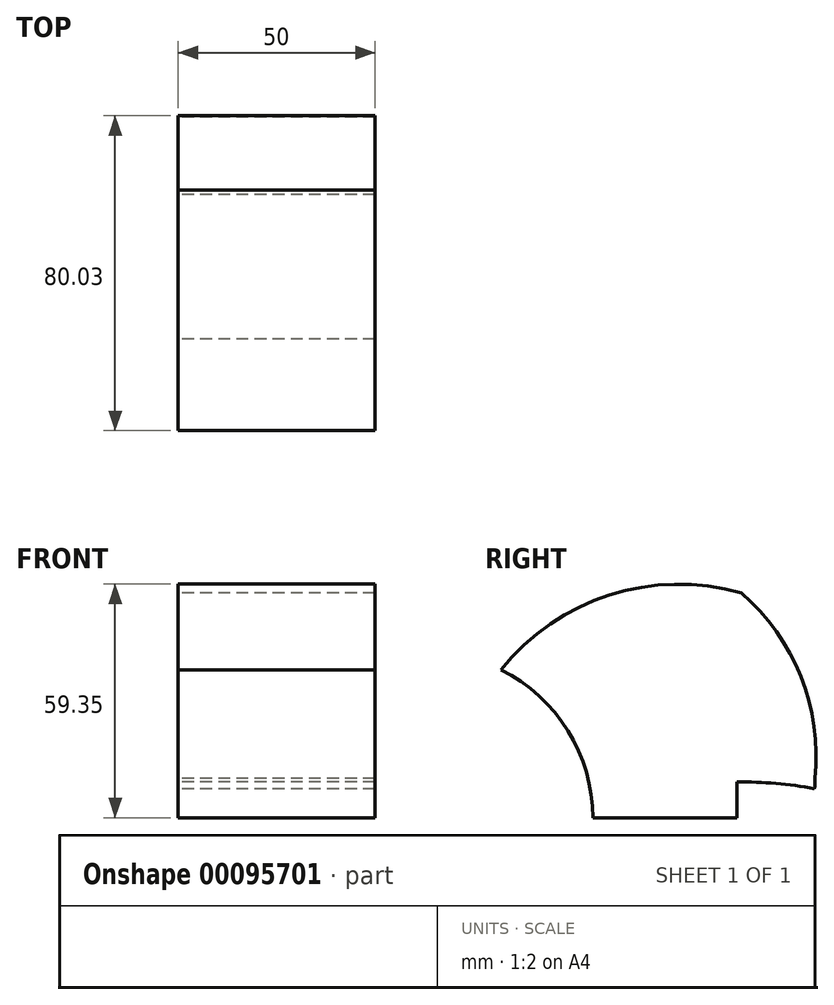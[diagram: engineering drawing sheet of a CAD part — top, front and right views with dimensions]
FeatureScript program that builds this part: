
annotation { "Feature Type Name" : "Feature", "Feature Type Description" : "" }
export const myFeature = defineFeature(function(context is Context, id is Id, definition is map)
    precondition{}
    {
        {
            var Q0;
            Q0=qCreatedBy(makeId("Right.planeOp"),FACE);
            var sketch = newSketch(context, id + "F0", { "sketchPlane" : qUnion([Q0])});
            skLineSegment(sketch, "E0.bottom", {"start": v(0, 0) * mm, "end": v(36.6, 0) * mm});
            skLineSegment(sketch, "E0.top", {"start": v(0, 28.9) * mm, "end": v(36.6, 28.9) * mm});
            skLineSegment(sketch, "E0.left", {"start": v(0, 0) * mm, "end": v(0, 28.9) * mm});
            skLineSegment(sketch, "E0.right", {"start": v(36.6, 0) * mm, "end": v(36.6, 28.9) * mm});
            skCircle(sketch, "E1", {"center": v(17.13, 14.67) * mm, "radius": 13.97 * mm});
            skArc(sketch, "E2", {"start": v(56.34, 7.4) * mm, "mid": v(51.19, 22.49) * mm, "end": v(36.6, 28.9) * mm});
            skArc(sketch, "E3", {"start": v(56.34, 7.4) * mm, "mid": v(46.5, 8.72) * mm, "end": v(36.6, 9.08) * mm});
            skArc(sketch, "E4", {"start": v(0, 28.9) * mm, "mid": v(-10.5, 36.4) * mm, "end": v(-23.34, 37.58) * mm});
            skArc(sketch, "E5", {"start": v(37.74, 57.16) * mm, "mid": v(4.25, 56.59) * mm, "end": v(-23.34, 37.58) * mm});
            skArc(sketch, "E6", {"start": v(56.4, 9.98) * mm, "mid": v(52.84, 35.86) * mm, "end": v(37.74, 57.16) * mm});
            skArc(sketch, "E7", {"start": v(0, 0) * mm, "mid": v(-6.3, 22.12) * mm, "end": v(-23.34, 37.58) * mm});
            skLineSegment(sketch, "E8", {"start": v(36.6, 0) * mm, "end": v(0, -26.64) * mm});
            skLineSegment(sketch, "E9", {"start": v(0, -2.2) * mm, "end": v(0, -26.64) * mm});
            skPoint(sketch, "E10.endSnap0", {"position": v(0, -14.42) * mm});
            skSolve(sketch);
        }
        {
            var Q0;
            {var subQ1=sQuery(id+"F0.wireOp",EDGE,"E0.top");Q0=makeQuery(id+"F0.imprint","IMPRINT",FACE,{"disambiguationData":[TD([[makeQuery(id+"F0.imprint","IMPRINT",EDGE,{"derivedFrom":subQ1}),1.0]])]});}
            extrude(context, id + "F1", {"entities" : qUnion([Q0]), "depth" : 50 * mm});
        }
        {
            var Q0;
            {var subQ1=sQuery(id+"F0.wireOp",EDGE,"E0.top");Q0=makeQuery(id+"F0.imprint","IMPRINT",FACE,{"disambiguationData":[TD([[makeQuery(id+"F0.imprint","IMPRINT",EDGE,{"derivedFrom":subQ1}),1.0]])]});}
            var Q1;
            {var subQ3=sQuery(id+"F0.wireOp",EDGE,"E3");Q1=makeQuery(id+"F0.imprint","IMPRINT",FACE,{"disambiguationData":[TD([[makeQuery(id+"F0.imprint","IMPRINT",EDGE,{"derivedFrom":subQ3}),-1.0]])]});}
            var Q2;
            Q2=makeQuery(id+"F0.imprint","IMPRINT",FACE,{"disambiguationData":[TD([[makeQuery(id+"F0.imprint","IMPRINT",EDGE,{"derivedFrom":sQuery(id+"F0.wireOp",EDGE,"E1")}),1.0]])]});
            var Q3;
            {var subQ1=sQuery(id+"F0.wireOp",EDGE,"E0.bottom");Q3=makeQuery(id+"F0.imprint","IMPRINT",FACE,{"disambiguationData":[TD([[makeQuery(id+"F0.imprint","IMPRINT",EDGE,{"derivedFrom":subQ1}),1.0]])]});}
            var Q4;
            Q4=makeQuery(id+"F0.imprint","IMPRINT",FACE,{"disambiguationData":[TD([[makeQuery(id+"F0.imprint","IMPRINT",EDGE,{"derivedFrom":sQuery(id+"F0.wireOp",EDGE,"E0.left")}),1.0]])]});
            extrude(context, id + "F2", {"entities" : qUnion([Q0, Q1, Q2, Q3, Q4]), "operationType" : NewBodyOperationType.ADD, "depth" : 50 * mm});
        }
    });
